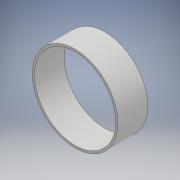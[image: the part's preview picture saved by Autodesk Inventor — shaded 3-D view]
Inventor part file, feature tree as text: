
AUTODESK INVENTOR PART (.ipt)
format: ipt  version: 2018 (Build 220112000, 112)  size: 102,400 bytes
history: native  units: mm
features: extrude x1, sketch x1
ambient origin geometry x8: Origin, YZ Plane, XZ Plane, XY Plane, X Axis, Y Axis, Z Axis, Center Point
bodies: Solid1 (feature_tree)
feature tree (2):
  extrude  "Extrusion1"  Depth=33.0mm
  sketch  "Sketch1"  dims[d0=90.0mm d1=95.0mm d2=33.0mm d3=0.0mm]
